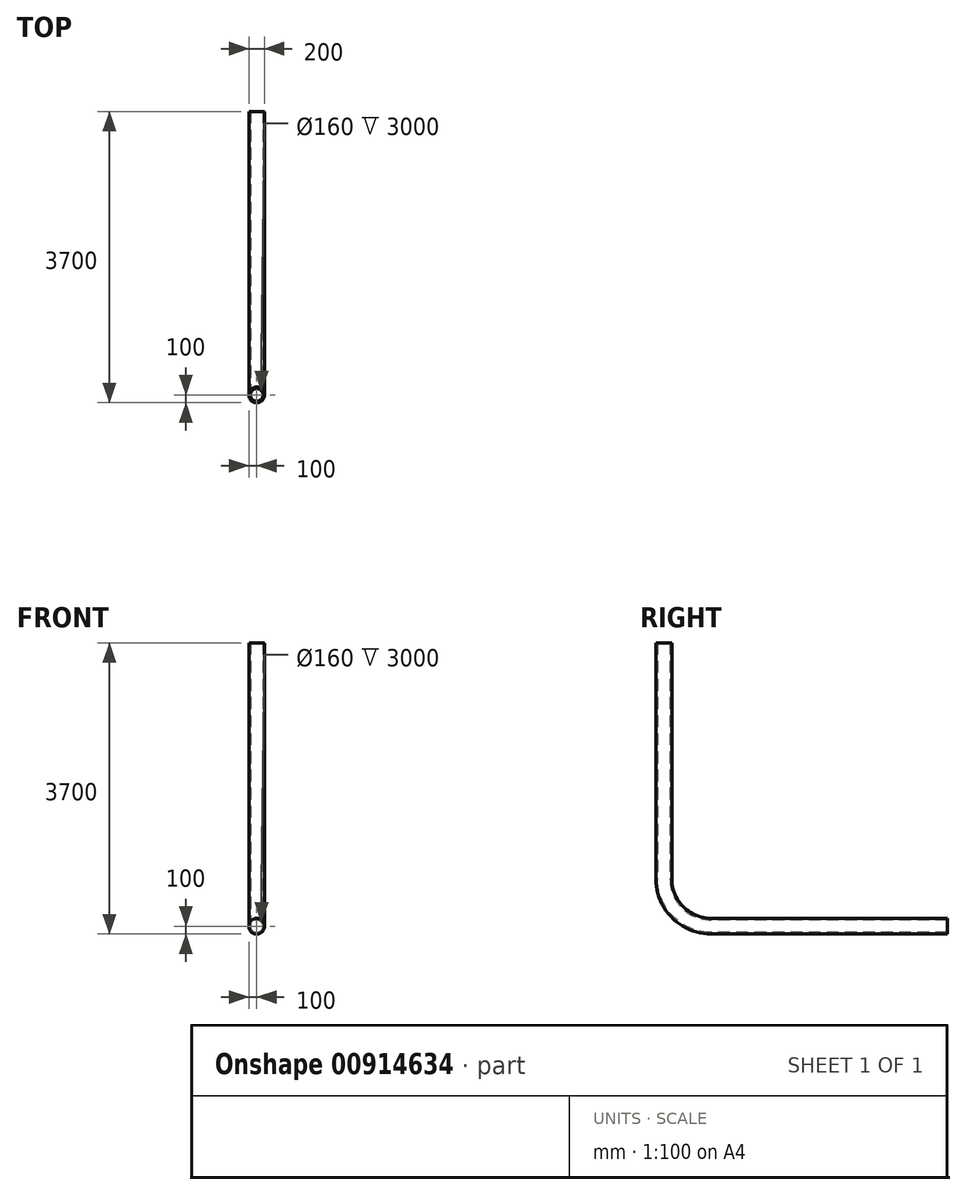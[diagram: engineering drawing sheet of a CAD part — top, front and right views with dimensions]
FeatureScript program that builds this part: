
annotation { "Feature Type Name" : "Feature", "Feature Type Description" : "" }
export const myFeature = defineFeature(function(context is Context, id is Id, definition is map)
    precondition{}
    {
        {
            var Q0;
            Q0=qCreatedBy(makeId("Front.planeOp"),FACE);
            var sketch = newSketch(context, id + "F0", { "sketchPlane" : qUnion([Q0])});
            skCircle(sketch, "E0", {"center": v(0, 0) * mm, "radius": 80 * mm});
            skCircle(sketch, "E1", {"center": v(0, 0) * mm, "radius": 100 * mm});
            skSolve(sketch);
        }
        {
            var Q0;
            Q0=qCreatedBy(makeId("Right.planeOp"),FACE);
            var sketch = newSketch(context, id + "F1", { "sketchPlane" : qUnion([Q0])});
            skLineSegment(sketch, "E2", {"start": v(0, 0) * mm, "end": v(0, 600) * mm, "construction": true});
            skLineSegment(sketch, "E3", {"start": v(-600, 600) * mm, "end": v(0, 600) * mm, "construction": true});
            skArc(sketch, "E4", {"start": v(-600, 600) * mm, "mid": v(-424.26, 175.74) * mm, "end": v(0, 0) * mm});
            skSolve(sketch);
        }
        {
            var Q0;
            Q0=makeQuery(id+"F0.imprint","IMPRINT",FACE,{"disambiguationData":[TD([[makeQuery(id+"F0.imprint","IMPRINT",EDGE,{"derivedFrom":sQuery(id+"F0.wireOp",EDGE,"E0")}),-1.0]])]});
            var Q1;
            Q1=sQuery(id+"F1.wireOp",EDGE,"E4");
            sweep(context, id + "F2", {"profiles" : qUnion([Q0]), "path" : qUnion([Q1])});
        }
        {
            var Q0;
            Q0=makeQuery(id+"F2.opSweep","CAP_FACE",FACE,{"disambiguationData":[OSD([sQuery(id+"F0.wireOp",EDGE,"E0"),sQuery(id+"F0.wireOp",EDGE,"E1"),sQuery(id+"F1.wireOp",VERTEX,"E4.end")])],"isStart":true});
            extrude(context, id + "F3", {"entities" : qUnion([Q0]), "operationType" : NewBodyOperationType.ADD, "depth" : 3000 * mm, "offsetDistance" : 25 * mm});
        }
        {
            var Q0;
            Q0=makeQuery(id+"F2.opSweep","CAP_FACE",FACE,{"disambiguationData":[OSD([sQuery(id+"F0.wireOp",EDGE,"E0"),sQuery(id+"F0.wireOp",EDGE,"E1"),sQuery(id+"F1.wireOp",VERTEX,"E4.start")])],"isStart":false});
            extrude(context, id + "F4", {"entities" : qUnion([Q0]), "operationType" : NewBodyOperationType.ADD, "depth" : 3000 * mm, "offsetDistance" : 25 * mm});
        }
    });
